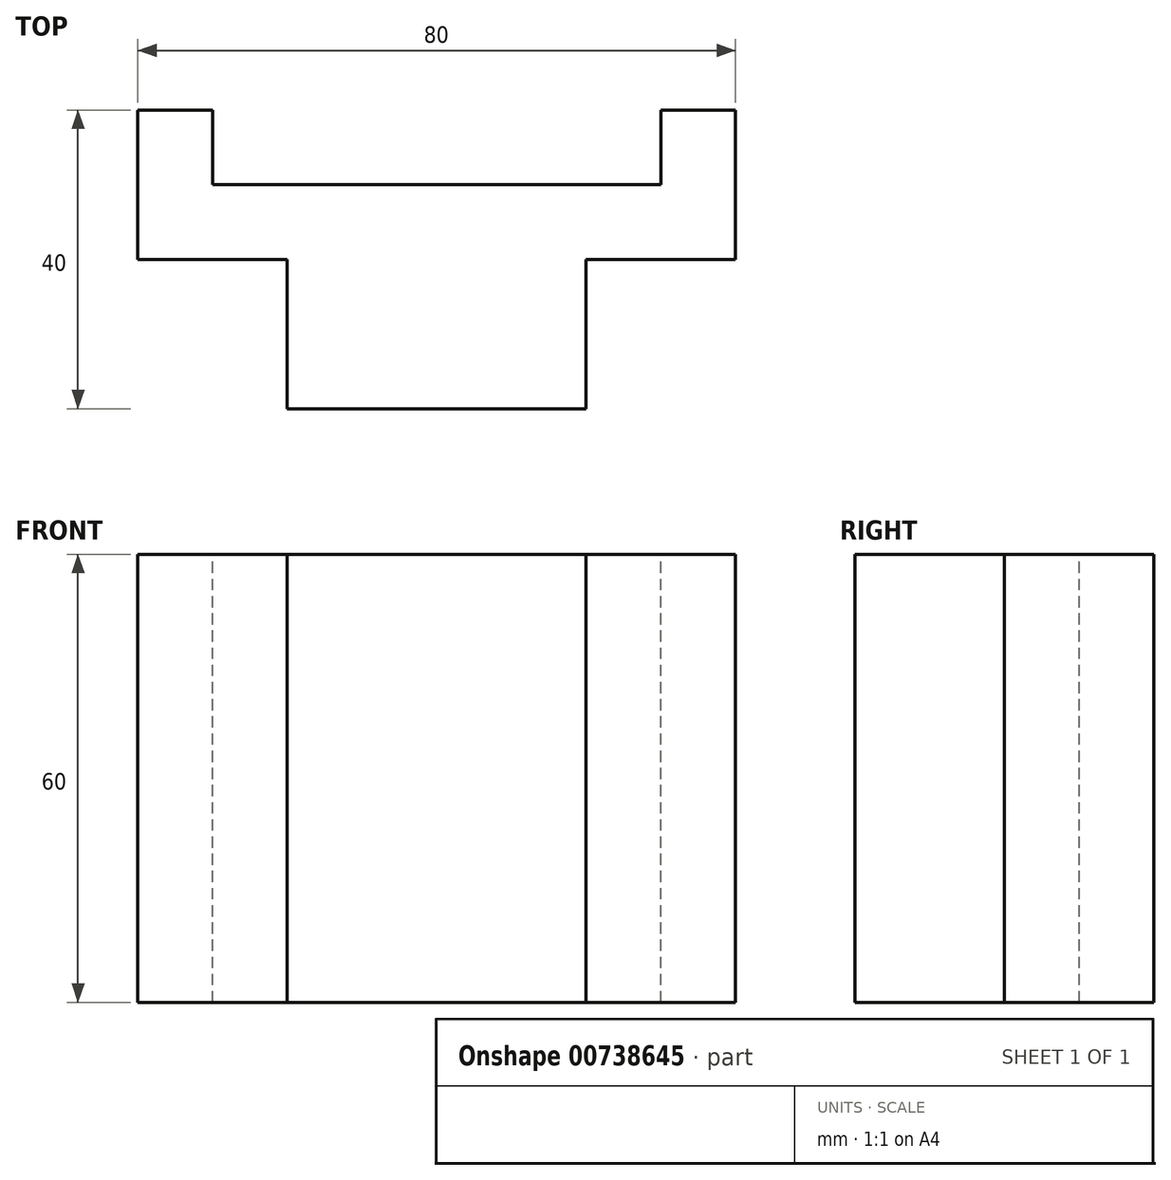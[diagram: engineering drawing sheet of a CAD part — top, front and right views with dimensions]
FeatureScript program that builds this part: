
annotation { "Feature Type Name" : "Feature", "Feature Type Description" : "" }
export const myFeature = defineFeature(function(context is Context, id is Id, definition is map)
    precondition{}
    {
        {
            var Q0;
            Q0=qCreatedBy(makeId("Front.planeOp"),FACE);
            var sketch = newSketch(context, id + "F0", { "sketchPlane" : qUnion([Q0])});
            skLineSegment(sketch, "E0.bottom", {"start": v(0, 0) * mm, "end": v(80, 0) * mm});
            skLineSegment(sketch, "E0.top", {"start": v(0, 60) * mm, "end": v(80, 60) * mm});
            skLineSegment(sketch, "E0.left", {"start": v(0, 0) * mm, "end": v(0, 60) * mm});
            skLineSegment(sketch, "E0.right", {"start": v(80, 0) * mm, "end": v(80, 60) * mm});
            skSolve(sketch);
        }
        {
            var Q0;
            Q0=makeQuery(id+"F0.imprint","IMPRINT",FACE,{"disambiguationData":[TD([[makeQuery(id+"F0.imprint","IMPRINT",EDGE,{"derivedFrom":sQuery(id+"F0.wireOp",EDGE,"E0.bottom")}),1.0]])]});
            extrude(context, id + "F1", {"entities" : qUnion([Q0]), "depth" : 40 * mm, "offsetDistance" : 25 * mm});
        }
        {
            var Q0;
            Q0=makeQuery(id+"F1.opExtrude","CAP_FACE",FACE,{"disambiguationData":[OSD([sQuery(id+"F0.wireOp",EDGE,"E0.bottom"),sQuery(id+"F0.wireOp",EDGE,"E0.top"),sQuery(id+"F0.wireOp",EDGE,"E0.left"),sQuery(id+"F0.wireOp",EDGE,"E0.right")])],"isStart":false});
            var sketch = newSketch(context, id + "F2", { "sketchPlane" : qUnion([Q0])});
            skLineSegment(sketch, "E1.bottom", {"start": v(0, 60) * mm, "end": v(20, 60) * mm});
            skLineSegment(sketch, "E1.top", {"start": v(0, 0) * mm, "end": v(20, 0) * mm});
            skLineSegment(sketch, "E1.left", {"start": v(0, 60) * mm, "end": v(0, 0) * mm});
            skLineSegment(sketch, "E1.right", {"start": v(20, 60) * mm, "end": v(20, 0) * mm});
            skLineSegment(sketch, "E2.bottom", {"start": v(80, 60) * mm, "end": v(60, 60) * mm});
            skLineSegment(sketch, "E2.top", {"start": v(80, 0) * mm, "end": v(60, 0) * mm});
            skLineSegment(sketch, "E2.left", {"start": v(80, 60) * mm, "end": v(80, 0) * mm});
            skLineSegment(sketch, "E2.right", {"start": v(60, 60) * mm, "end": v(60, 0) * mm});
            skSolve(sketch);
        }
        {
            var Q0;
            Q0=makeQuery(id+"F2.imprint","IMPRINT",FACE,{"disambiguationData":[TD([[makeQuery(id+"F2.imprint","IMPRINT",EDGE,{"derivedFrom":sQuery(id+"F2.wireOp",EDGE,"E1.bottom")}),-1.0]])]});
            var Q1;
            Q1=makeQuery(id+"F2.imprint","IMPRINT",FACE,{"disambiguationData":[TD([[makeQuery(id+"F2.imprint","IMPRINT",EDGE,{"derivedFrom":sQuery(id+"F2.wireOp",EDGE,"E2.bottom")}),-1.0]])]});
            extrude(context, id + "F3", {"entities" : qUnion([Q0, Q1]), "operationType" : NewBodyOperationType.REMOVE, "oppositeDirection" : true, "depth" : 20 * mm, "offsetDistance" : 25 * mm});
        }
        {
            var Q0;
            Q0=makeQuery(id+"F1.opExtrude","CAP_FACE",FACE,{"disambiguationData":[OSD([sQuery(id+"F0.wireOp",EDGE,"E0.bottom"),sQuery(id+"F0.wireOp",EDGE,"E0.top"),sQuery(id+"F0.wireOp",EDGE,"E0.left"),sQuery(id+"F0.wireOp",EDGE,"E0.right")])],"isStart":true});
            var sketch = newSketch(context, id + "F4", { "sketchPlane" : qUnion([Q0])});
            skLineSegment(sketch, "E3.bottom", {"start": v(-10, 0) * mm, "end": v(-70, 0) * mm});
            skLineSegment(sketch, "E3.top", {"start": v(-10, 60) * mm, "end": v(-70, 60) * mm});
            skLineSegment(sketch, "E3.left", {"start": v(-10, 0) * mm, "end": v(-10, 60) * mm});
            skLineSegment(sketch, "E3.right", {"start": v(-70, 0) * mm, "end": v(-70, 60) * mm});
            skSolve(sketch);
        }
        {
            var Q0;
            Q0=makeQuery(id+"F4.imprint","IMPRINT",FACE,{"disambiguationData":[TD([[makeQuery(id+"F4.imprint","IMPRINT",EDGE,{"derivedFrom":sQuery(id+"F4.wireOp",EDGE,"E3.bottom")}),-1.0]])]});
            extrude(context, id + "F5", {"entities" : qUnion([Q0]), "operationType" : NewBodyOperationType.REMOVE, "oppositeDirection" : true, "depth" : 10 * mm, "offsetDistance" : 25 * mm});
        }
    });
